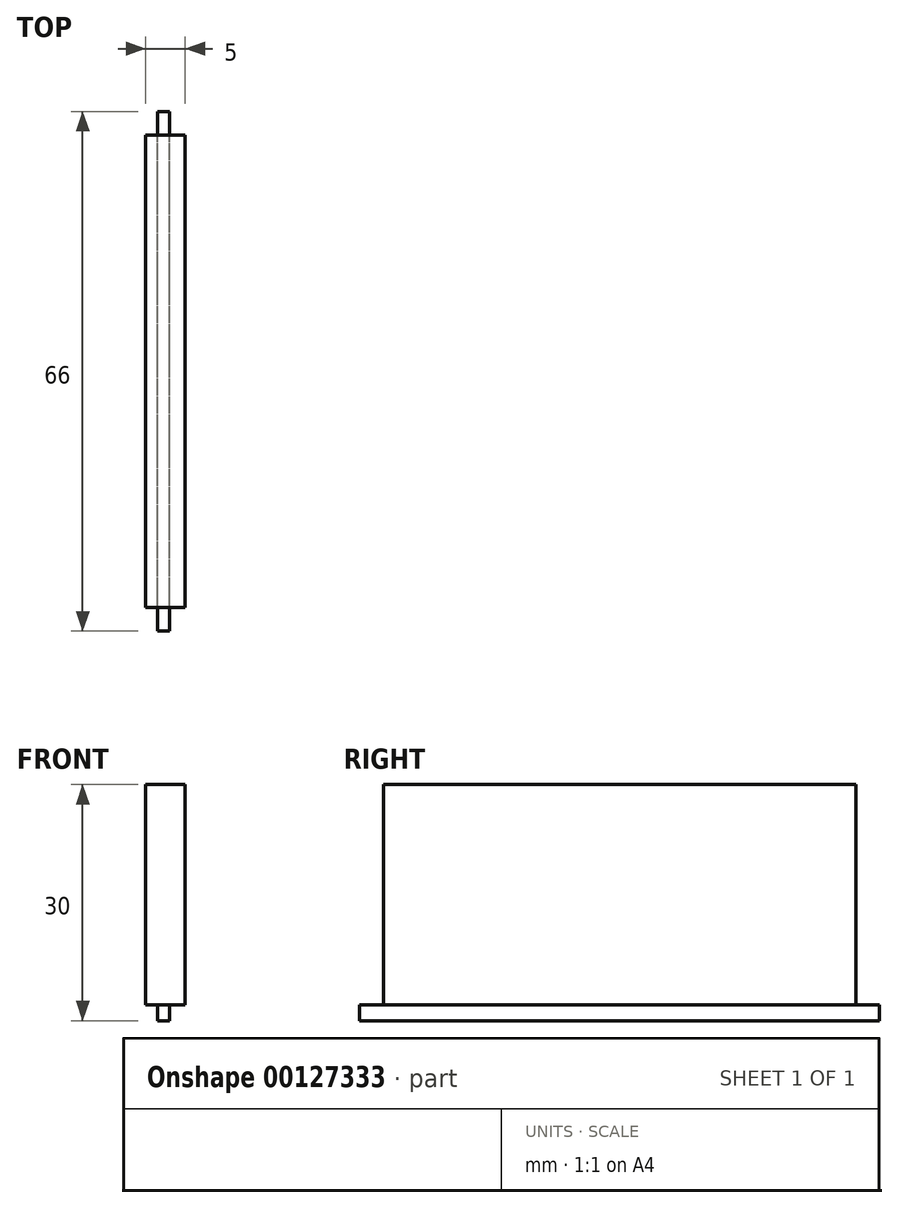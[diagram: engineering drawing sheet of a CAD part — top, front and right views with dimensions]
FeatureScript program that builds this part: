
annotation { "Feature Type Name" : "Feature", "Feature Type Description" : "" }
export const myFeature = defineFeature(function(context is Context, id is Id, definition is map)
    precondition{}
    {
        {
            var Q0;
            Q0=qCreatedBy(makeId("Top.planeOp"),FACE);
            var sketch = newSketch(context, id + "F0", { "sketchPlane" : qUnion([Q0])});
            skLineSegment(sketch, "E0.bottom", {"start": v(2.5, -30) * mm, "end": v(-2.5, -30) * mm});
            skLineSegment(sketch, "E0.top", {"start": v(2.5, 30) * mm, "end": v(-2.5, 30) * mm});
            skLineSegment(sketch, "E0.left", {"start": v(2.5, -30) * mm, "end": v(2.5, 30) * mm});
            skLineSegment(sketch, "E0.right", {"start": v(-2.5, -30) * mm, "end": v(-2.5, 30) * mm});
            skPoint(sketch, "E0.middle", {"position": v(0, 0) * mm});
            skLineSegment(sketch, "E1.bottom", {"start": v(-1, -30) * mm, "end": v(0.5, -30) * mm});
            skLineSegment(sketch, "E1.top", {"start": v(-1, -33) * mm, "end": v(0.5, -33) * mm});
            skLineSegment(sketch, "E1.left", {"start": v(-1, -30) * mm, "end": v(-1, -33) * mm});
            skLineSegment(sketch, "E1.right", {"start": v(0.5, -30) * mm, "end": v(0.5, -33) * mm});
            skLineSegment(sketch, "E2", {"start": v(0.5, -31.5) * mm, "end": v(2.5, -31.5) * mm});
            skLineSegment(sketch, "E3.bottom", {"start": v(-1, 30) * mm, "end": v(0.5, 30) * mm});
            skLineSegment(sketch, "E3.top", {"start": v(-1, 33) * mm, "end": v(0.5, 33) * mm});
            skLineSegment(sketch, "E3.left", {"start": v(-1, 30) * mm, "end": v(-1, 33) * mm});
            skLineSegment(sketch, "E3.right", {"start": v(0.5, 30) * mm, "end": v(0.5, 33) * mm});
            skLineSegment(sketch, "E4", {"start": v(0.5, 31.5) * mm, "end": v(2.5, 31.5) * mm});
            skSolve(sketch);
        }
        {
            var Q0;
            {var subQ3=sQuery(id+"F0.wireOp",EDGE,"E0.left");Q0=makeQuery(id+"F0.imprint","IMPRINT",FACE,{"disambiguationData":[TD([[makeQuery(id+"F0.imprint","IMPRINT",EDGE,{"derivedFrom":subQ3}),1.0]])]});}
            var Q1;
            {var subQ1=sQuery(id+"F0.wireOp",EDGE,"E3.bottom");Q1=makeQuery(id+"F0.imprint","IMPRINT",FACE,{"disambiguationData":[TD([[makeQuery(id+"F0.imprint","IMPRINT",EDGE,{"derivedFrom":subQ1}),1.0]])]});}
            var Q2;
            {var subQ1=sQuery(id+"F0.wireOp",EDGE,"E1.bottom");Q2=makeQuery(id+"F0.imprint","IMPRINT",FACE,{"disambiguationData":[TD([[makeQuery(id+"F0.imprint","IMPRINT",EDGE,{"derivedFrom":subQ1}),-1.0]])]});}
            extrude(context, id + "F1", {"entities" : qUnion([Q0, Q1, Q2]), "oppositeDirection" : true, "depth" : 28 * mm});
        }
        {
            var Q0;
            Q0=makeQuery(id+"F1.opExtrude","CAP_FACE",FACE,{"disambiguationData":[OSD([sQuery(id+"F0.wireOp",EDGE,"E0.bottom"),sQuery(id+"F0.wireOp",EDGE,"E0.top"),sQuery(id+"F0.wireOp",EDGE,"E0.left"),sQuery(id+"F0.wireOp",EDGE,"E0.right"),sQuery(id+"F0.wireOp",EDGE,"E1.top"),sQuery(id+"F0.wireOp",EDGE,"E1.left"),sQuery(id+"F0.wireOp",EDGE,"E1.right"),sQuery(id+"F0.wireOp",EDGE,"E3.top"),sQuery(id+"F0.wireOp",EDGE,"E3.left"),sQuery(id+"F0.wireOp",EDGE,"E3.right")])],"isStart":false});
            var sketch = newSketch(context, id + "F2", { "sketchPlane" : qUnion([Q0])});
            skLineSegment(sketch, "E5.bottom", {"start": v(0.5, 33) * mm, "end": v(-1, 33) * mm});
            skLineSegment(sketch, "E5.top", {"start": v(0.5, -33) * mm, "end": v(-1, -33) * mm});
            skLineSegment(sketch, "E5.left", {"start": v(0.5, 33) * mm, "end": v(0.5, -33) * mm});
            skLineSegment(sketch, "E5.right", {"start": v(-1, 33) * mm, "end": v(-1, -33) * mm});
            skSolve(sketch);
        }
        {
            var Q0;
            Q0 = qSketchRegion(id + "F2", true);
            var Q1;
            {var subQ9=sQuery(id+"F2.wireOp",EDGE,"E5.bottom");Q1=makeQuery(id+"F2.imprint","IMPRINT",FACE,{"disambiguationData":[TD([[makeQuery(id+"F2.imprint","IMPRINT",EDGE,{"derivedFrom":subQ9}),-1.0]])]});}
            extrude(context, id + "F3", {"entities" : qUnion([Q0, Q1]), "operationType" : NewBodyOperationType.ADD, "depth" : 2 * mm});
        }
    });
